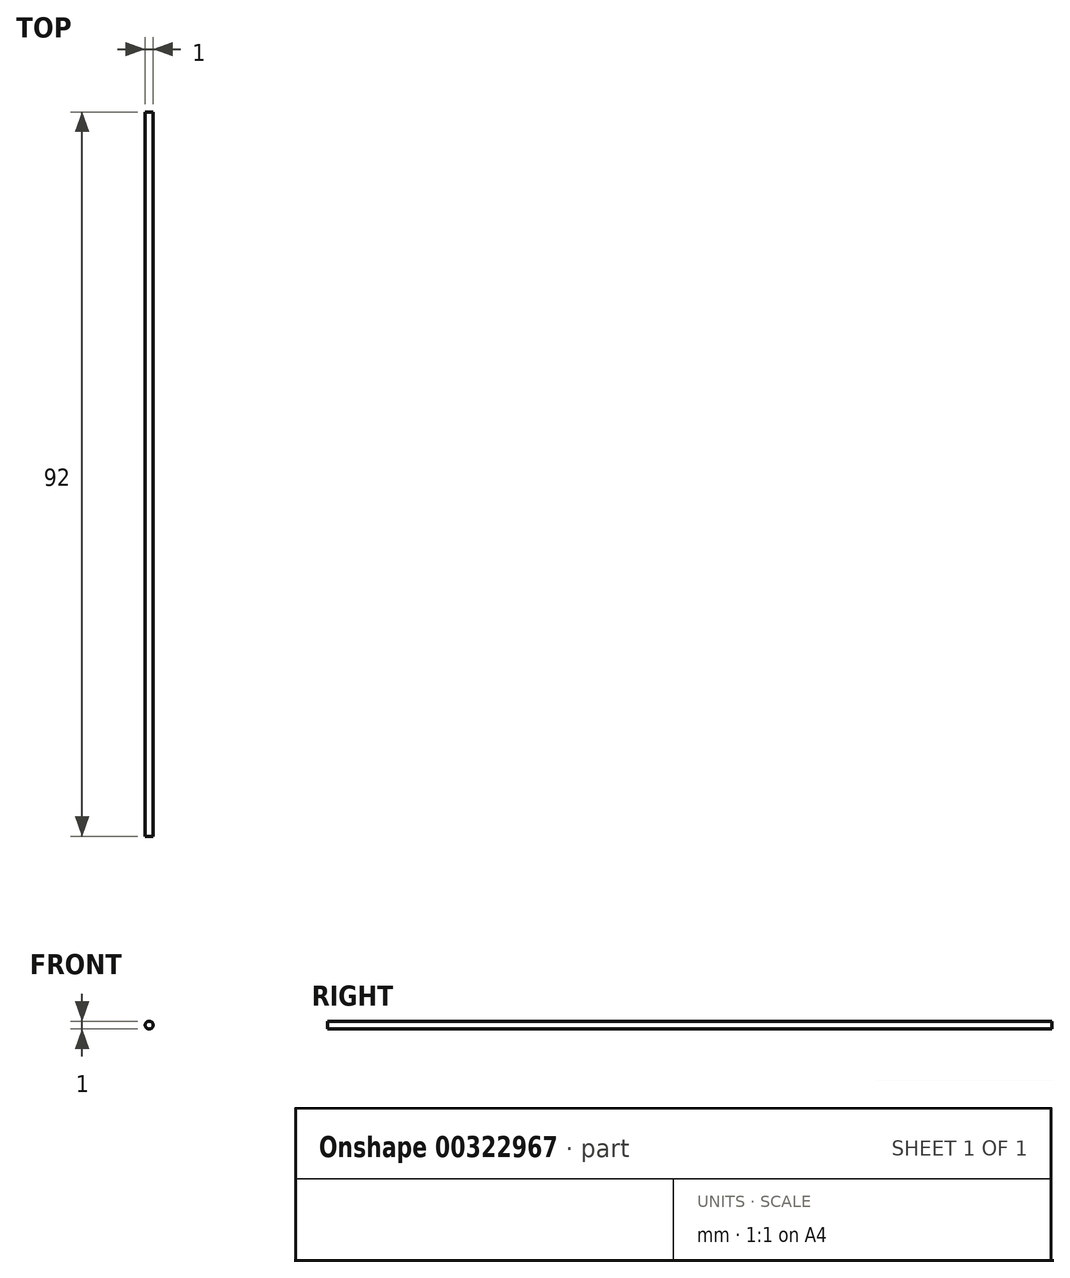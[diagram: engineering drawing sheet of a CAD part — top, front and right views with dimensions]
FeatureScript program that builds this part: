
annotation { "Feature Type Name" : "Feature", "Feature Type Description" : "" }
export const myFeature = defineFeature(function(context is Context, id is Id, definition is map)
    precondition{}
    {
        {
            var Q0;
            Q0=qCreatedBy(makeId("Front.planeOp"),FACE);
            var sketch = newSketch(context, id + "F0", { "sketchPlane" : qUnion([Q0])});
            skCircle(sketch, "E0", {"center": v(0, 0) * mm, "radius": 0.5 * mm});
            skSolve(sketch);
        }
        {
            var Q0;
            Q0 = qSketchRegion(id + "F0", true);
            extrude(context, id + "F1", {"entities" : qUnion([Q0]), "depth" : 92 * mm});
        }
    });
